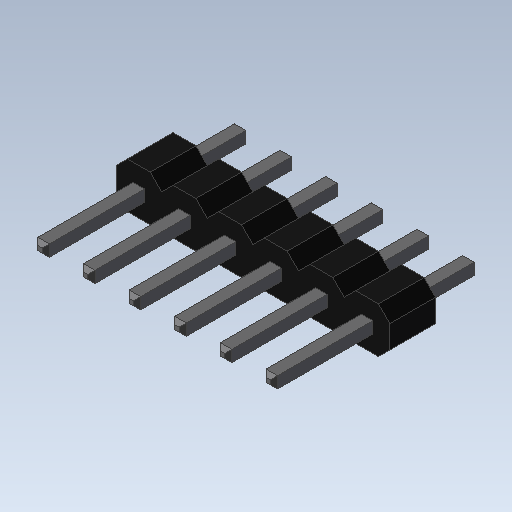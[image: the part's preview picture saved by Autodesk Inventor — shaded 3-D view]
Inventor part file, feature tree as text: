
AUTODESK INVENTOR PART (.ipt)
format: ipt  version: 2020 (Build 240168000, 168)  size: 174,592 bytes
history: imported  units: in
note: dims shown in document units (in); Inventor stores cm internally (conversion verified against a paired STEP export)
features: imported_body x1
ambient origin geometry x8: Origin, YZ Plane, XZ Plane, XY Plane, X Axis, Y Axis, Z Axis, Center Point
bodies: Solid1 (imported_parasolid), Body2 (imported_parasolid)
feature tree (1):
  imported_body  NMx_Import_Brep_tag  [imported B-rep: ~148 faces, bbox_mm=[15.24, 2.54, 11.34]]
